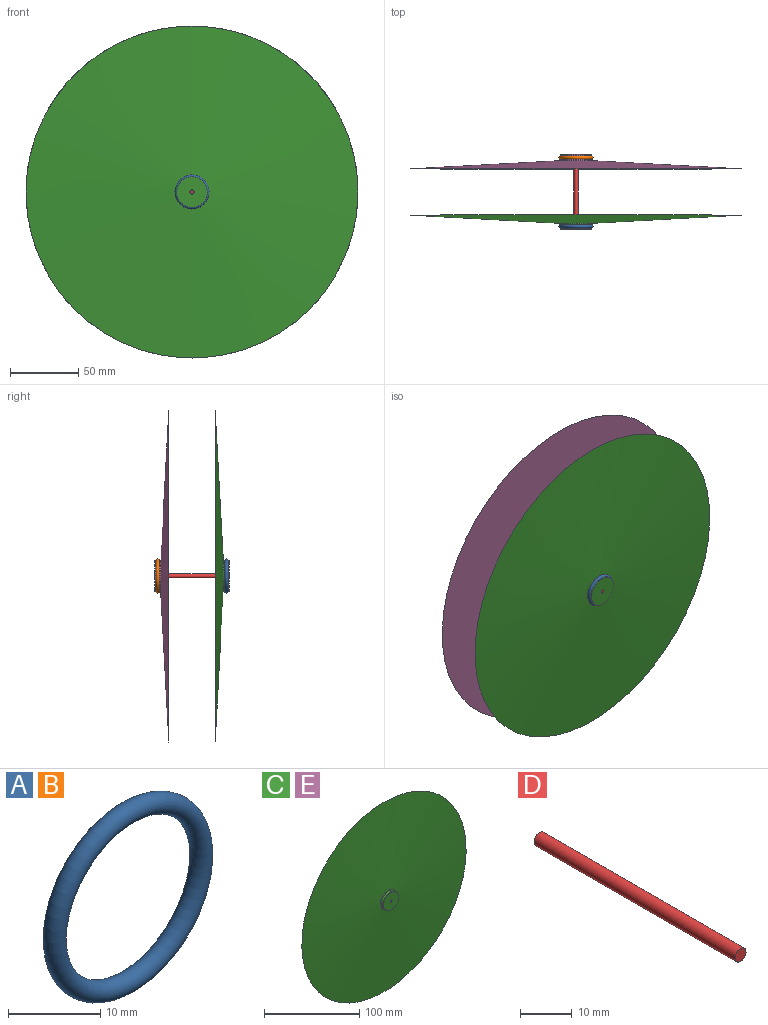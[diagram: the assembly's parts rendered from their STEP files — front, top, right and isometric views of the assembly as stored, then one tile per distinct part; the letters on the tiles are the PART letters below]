
ASSEMBLY  parts=5 mates=3
PART A: 1 faces, bbox 27.1x2.5x27.1 mm
  f0: torus R=11.25mm, axis (0,-1,0), area 555.2mm2
PART B: same geometry as A
PART C: 7 faces, bbox 243.6x10.5x243.6 mm
  f0: plane 243.63x243.63mm, normal (0,1,0), area 46611.9mm2, adj f1,f6
  f1: cone r=11.25mm half-angle=86.9deg, axis (0,1,0), area 46289.4mm2, adj f0,f2
  f2: cylinder r=11.25mm len=22.5mm, axis (0,1,0), area 70.7mm2, adj f1,f3
  f3: torus R=11.25mm, axis (0,1,0), area 257.9mm2, adj f2,f4
  f4: cylinder r=11.25mm len=22.5mm, axis (0,1,0), area 70.7mm2, adj f3,f5
  f5: plane 22.5x22.5mm, normal (0,-1,0), area 390.5mm2, adj f4,f6
  f6: cylinder r=1.5mm len=10.5mm, axis (0,-1,0), area 99mm2, adj f0,f5
PART D: 3 faces, bbox 3x55x3 mm
  f0: plane 3x3mm, normal (0,-1,0), area 7.1mm2, adj f2
  f1: plane 3x3mm, normal (0,1,0), area 7.1mm2, adj f2
  f2: cylinder r=1.5mm len=55mm, axis (0,1,0), area 518.4mm2, adj f0,f1
PART E: same geometry as C
PLACE A t=(20,80.5,25)mm
PLACE B t=(20,131,25)mm
PLACE C t=(-6.58,9.27,-3.9)mm
PLACE D at identity
PLACE E rot(axis=(1,0,0),180deg) t=(-6.58,5.73,88.9)mm
MATE fastened E.f1 <-> D.f2  axis (0,1,0) through (-142.5,35,42.5)mm
MATE fastened A.f0 <-> C.f1  axis (0,-1,0) through (-142.5,-17.75,42.5)mm
MATE fastened B.f0 <-> E.f1  axis (0,-1,0) through (-142.5,32.75,42.5)mm
